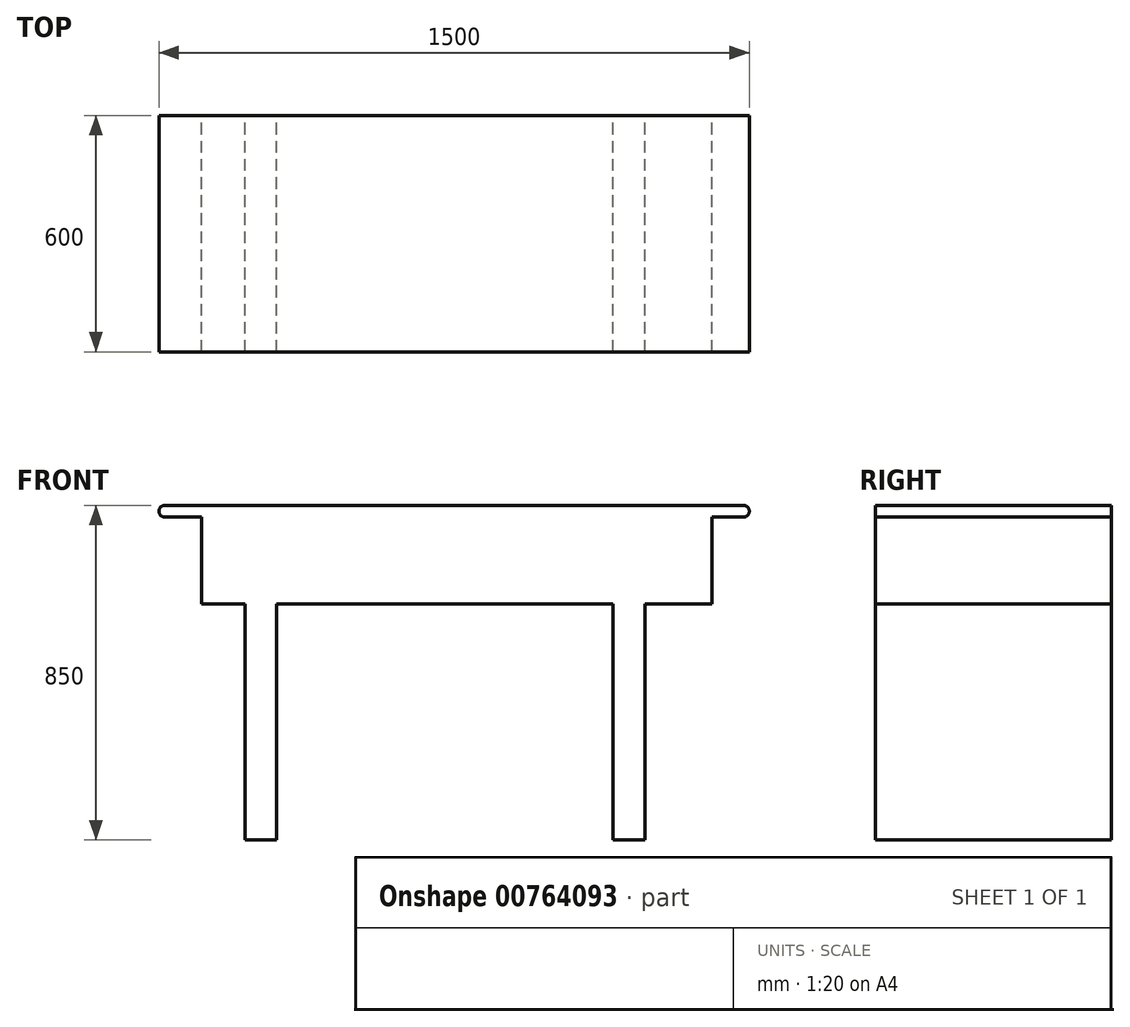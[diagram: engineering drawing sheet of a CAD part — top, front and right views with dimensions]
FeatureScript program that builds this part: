
annotation { "Feature Type Name" : "Feature", "Feature Type Description" : "" }
export const myFeature = defineFeature(function(context is Context, id is Id, definition is map)
    precondition{}
    {
        {
            var Q0;
            Q0=qCreatedBy(makeId("Front.planeOp"),FACE);
            var sketch = newSketch(context, id + "F0", { "sketchPlane" : qUnion([Q0])});
            skArc(sketch, "E0", {"start": v(-724.1, 41.69) * mm, "mid": v(-739.1, 26.69) * mm, "end": v(-724.1, 11.69) * mm});
            skArc(sketch, "E1", {"start": v(745.9, 11.69) * mm, "mid": v(760.9, 26.69) * mm, "end": v(745.9, 41.69) * mm});
            skLineSegment(sketch, "E2", {"start": v(-724.1, 41.69) * mm, "end": v(745.9, 41.69) * mm});
            skLineSegment(sketch, "E3", {"start": v(745.9, 11.69) * mm, "end": v(665.57, 11.69) * mm});
            skLineSegment(sketch, "E4", {"start": v(-630.47, 11.69) * mm, "end": v(-630.47, -209.2) * mm});
            skLineSegment(sketch, "E5", {"start": v(-630.47, -209.2) * mm, "end": v(-520.36, -209.2) * mm});
            skLineSegment(sketch, "E6", {"start": v(665.57, -209.2) * mm, "end": v(665.57, 11.69) * mm});
            skLineSegment(sketch, "E7", {"start": v(-520.36, -209.2) * mm, "end": v(-520.36, -808.31) * mm});
            skLineSegment(sketch, "E8", {"start": v(-520.36, -808.31) * mm, "end": v(-440.36, -808.31) * mm});
            skLineSegment(sketch, "E9", {"start": v(-440.36, -808.31) * mm, "end": v(-440.36, -209.2) * mm});
            skLineSegment(sketch, "E10", {"start": v(495.15, -209.2) * mm, "end": v(495.15, -808.31) * mm});
            skLineSegment(sketch, "E11", {"start": v(495.15, -808.31) * mm, "end": v(415.15, -808.31) * mm});
            skLineSegment(sketch, "E12", {"start": v(415.15, -808.31) * mm, "end": v(415.15, -209.2) * mm});
            skLineSegment(sketch, "E13.trimOffspring", {"start": v(-630.47, 11.69) * mm, "end": v(-724.1, 11.69) * mm});
            skLineSegment(sketch, "E14.trimOffspring", {"start": v(-440.36, -209.2) * mm, "end": v(415.15, -209.2) * mm});
            skLineSegment(sketch, "E15.trimOffspring", {"start": v(495.15, -209.2) * mm, "end": v(665.57, -209.2) * mm});
            skSolve(sketch);
        }
        {
            var Q0;
            Q0=makeQuery(id+"F0.imprint","IMPRINT",FACE,{"disambiguationData":[TD([[makeQuery(id+"F0.imprint","IMPRINT",EDGE,{"derivedFrom":sQuery(id+"F0.wireOp",EDGE,"E0")}),1.0]])]});
            extrude(context, id + "F1", {"entities" : qUnion([Q0]), "depth" : 600 * mm, "offsetDistance" : 25 * mm});
        }
    });
